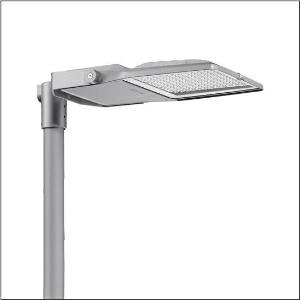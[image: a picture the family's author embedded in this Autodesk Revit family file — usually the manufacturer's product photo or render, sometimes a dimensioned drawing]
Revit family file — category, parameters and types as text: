
# Revit family: floodlight_fl_21_iq_midi___pl43_5xa7782f4a3a_c232
name_source: partatom
category: Lighting Fixtures
units: mm (PartAtom-declared; Revit-internal decimal feet)

## family parameters
Cut with Voids When Loaded = No
Host = Face
Light Source = No
Part Type = Normal
Room Calculation Point = No
Round Connector Dimension = Use Diameter
Shared = No

## types (1)
- --- (1 x LED, 38290 lm, 270.2 W, 4000K)
    Apparent Load = 270 VA
    CIE Flux Codes = 27 78 99 100 100
    Color Rendering = 70
    Color Temperature = 4000K
    Default Elevation = 1800 mm
    Description = Floodlight FL 21 iQ midi, floodlight, primary light control with lens, of PMMA, primary optical cover: protective disc, of toughened safety glass, transparent, light distribution: PL43, light emission: direct distribution, installation type: surface-mounted, LED, High Power LED, rated luminous flux: 38.290lm, luminous efficacy: 142lm/W, light colour: 740, colour temperature: 4000K, control gear: ECG iQ, control: optimised constant luminous flux control (CLO 2.0), Desk-Remote (wireless, voltage-free reading and setting of iQ features in the workshop via application-optimized NFC function/RFID function), Smart-Wire, Night-Set, Temp-Guard, Auto-Match, Street-Remote, with terminal, 6-pole, mains connection: 220..240V, AC, 50/60Hz, start of lifetime: 270W, end of service life: 287W, reduction: 118W, luminaire housing, of diecast aluminium, powder-coated, Siteco® metallic grey (DB 702S), corrosivity category C5 mid according to DIN EN ISO 12944, sealing non-destructively replaceable, please order mast flange separately, mast bracket, of steel, galvanised, powder-coated, Siteco® metallic grey (DB 702S), protection rating (complete): IP66, insulation class (complete): insulation class II (safety insulation), certification: CE, protection symbol: D, impact resistance: IK08, permissible operating ambient temperature: -40..+40°C, permissible operating ambient temperature for outdoor applications: -40..+50°C, standard: DIN EN 12944, LABS conformity tested according to VDMA 24364:2018-05, packaging unit: 1 piece

Light Distribution: PL43
    Height = 76 mm
    Lamp = 1 x LED
    Lamp Light Flux = 38290 lm
    Lamp Power = 270.2 W
    Lamp count = 1
    Length = 657 mm
    Luminous efficacy = 142 lm/W
    Manufacturer = Siteco
    ModVariant = No
    Model = 5XA7782F4A3A
    Number of Poles = 1
    OnlyDefault = Yes
    Power Factor = 1
    Product Name = Floodlight FL 21 iQ midi | PL43
    Product group = floodlight | pylon annexe
    ProductGroupID = 6200
    Protection Class = Protection class II
    Protection Degree = IP 66
    RLX_Detail_Level = 1
    RLX_Emergency_Light_Flux = 0 lm
    RLX_Emergency_Type = 0
    RLX_Emergency_Type_DB = No
    RlxData = <blob elided: 153465 chars, md5=59da1d53>
    Socket = socket
    Standby Power = 0 W
    System Light Flux = 38290 lm
    System Power = 270 W
    Type Comments = factory setting: luminous flux: 100 % | dim-lin: 254 | 620 mA
    Type Image = l_1007123.jpg
    URL = http://relux.com
    VarID = @adj_034711
    Voltage = 0 V
    Weight = 0.00 kg
    Width = 442 mm

## geometry (parser evidence)
native form markers: Blend x4, Sweep x14
no freeform markers — native parametric forms only
